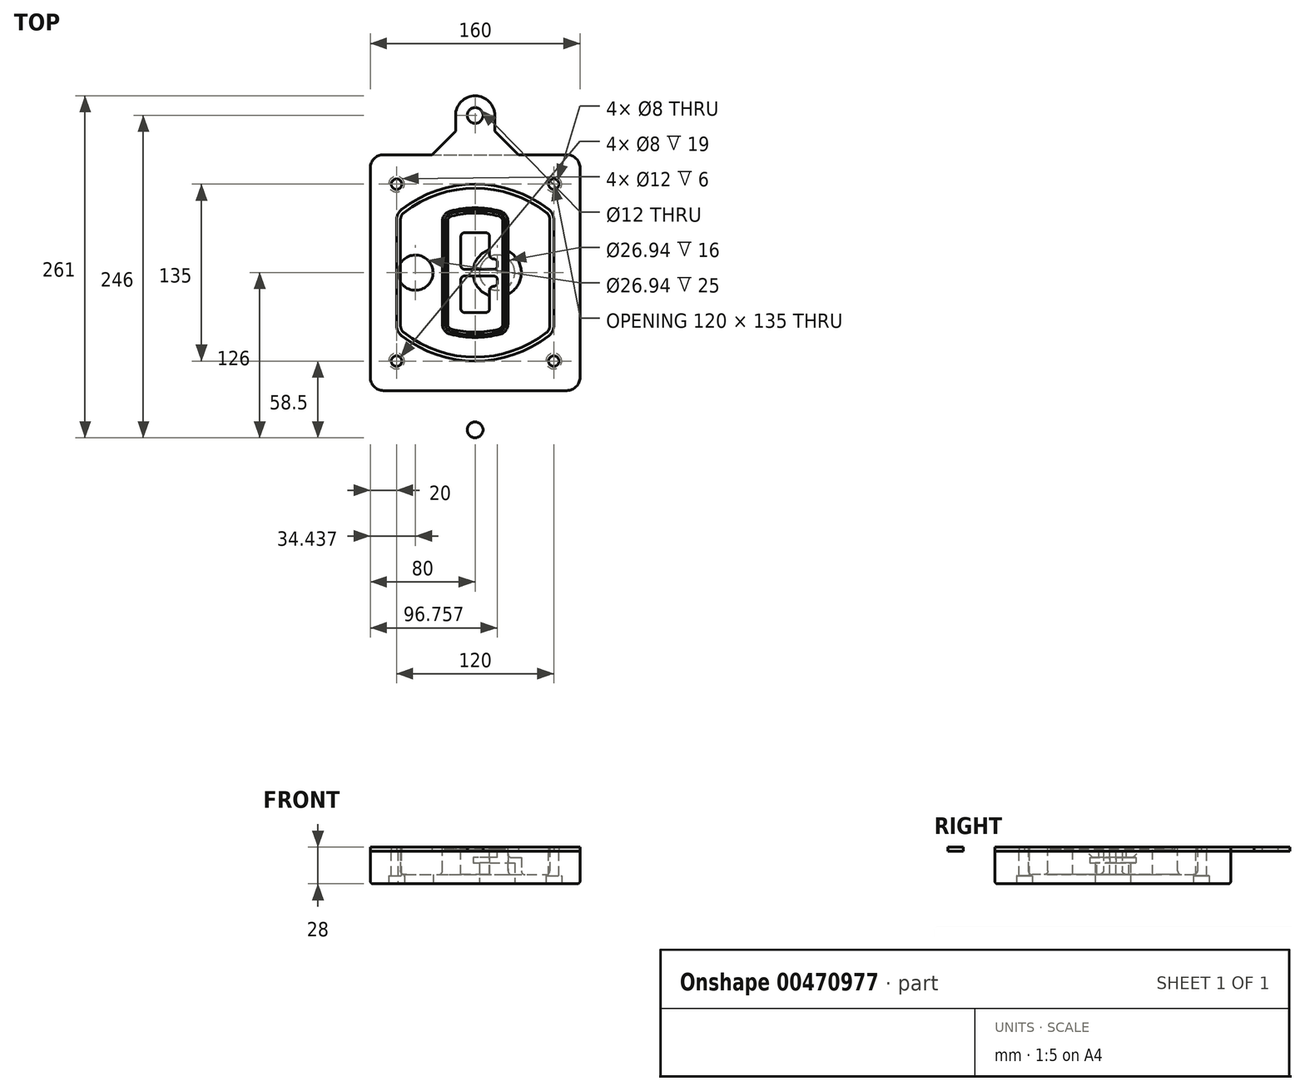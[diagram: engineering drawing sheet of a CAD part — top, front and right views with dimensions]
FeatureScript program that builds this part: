
annotation { "Feature Type Name" : "Feature", "Feature Type Description" : "" }
export const myFeature = defineFeature(function(context is Context, id is Id, definition is map)
    precondition{}
    {
        {
            var Q0;
            Q0=qCreatedBy(makeId("Top.planeOp"),FACE);
            var sketch = newSketch(context, id + "F0", { "sketchPlane" : qUnion([Q0])});
            skPoint(sketch, "E0.rect.middle", {"position": v(0, 0) * mm});
            skLineSegment(sketch, "E1.bottom", {"start": v(-70, -90) * mm, "end": v(70, -90) * mm});
            skLineSegment(sketch, "E1.top", {"start": v(-70, 90) * mm, "end": v(70, 90) * mm});
            skLineSegment(sketch, "E1.left", {"start": v(-80, -80) * mm, "end": v(-80, 80) * mm});
            skLineSegment(sketch, "E1.right", {"start": v(80, -80) * mm, "end": v(80, 80) * mm});
            skLineSegment(sketch, "E2", {"start": v(-80, 90) * mm, "end": v(80, -90) * mm, "construction": true});
            skLineSegment(sketch, "E3", {"start": v(80, 90) * mm, "end": v(-80, -90) * mm, "construction": true});
            skCircle(sketch, "E4", {"center": v(-60, 67.5) * mm, "radius": 4 * mm});
            skCircle(sketch, "E5", {"center": v(60, 67.5) * mm, "radius": 4 * mm});
            skCircle(sketch, "E6", {"center": v(60, -67.5) * mm, "radius": 4 * mm});
            skCircle(sketch, "E7", {"center": v(-60, -67.5) * mm, "radius": 4 * mm});
            skLineSegment(sketch, "E8", {"start": v(-60, 67.5) * mm, "end": v(60, 67.5) * mm, "construction": true});
            skLineSegment(sketch, "E9", {"start": v(60, 67.5) * mm, "end": v(60, -67.5) * mm, "construction": true});
            skLineSegment(sketch, "E10", {"start": v(60, -67.5) * mm, "end": v(-60, -67.5) * mm, "construction": true});
            skLineSegment(sketch, "E11", {"start": v(-60, -67.5) * mm, "end": v(-60, 67.5) * mm, "construction": true});
            skLineSegment(sketch, "E12", {"start": v(-60, 40.3) * mm, "end": v(-60, -40.3) * mm});
            skLineSegment(sketch, "E13", {"start": v(60, 40.3) * mm, "end": v(60, -40.3) * mm});
            skArc(sketch, "E14", {"start": v(56.15, 48.18) * mm, "mid": v(0, 67.5) * mm, "end": v(-56.15, 48.18) * mm});
            skArc(sketch, "E15", {"start": v(-56.15, -48.18) * mm, "mid": v(0, -67.5) * mm, "end": v(56.15, -48.18) * mm});
            skLineSegment(sketch, "E16", {"start": v(-60, 0) * mm, "end": v(60, 0) * mm, "construction": true});
            skPoint(sketch, "E17.visualSharp", {"position": v(-60, -45) * mm});
            skArc(sketch, "E17.filletArc", {"start": v(-60, -40.3) * mm, "mid": v(-58.99, -44.68) * mm, "end": v(-56.15, -48.18) * mm});
            skPoint(sketch, "E18.visualSharp", {"position": v(-60, 45) * mm});
            skArc(sketch, "E18.filletArc", {"start": v(-56.15, 48.18) * mm, "mid": v(-58.99, 44.68) * mm, "end": v(-60, 40.3) * mm});
            skPoint(sketch, "E19.visualSharp", {"position": v(60, 45) * mm});
            skArc(sketch, "E19.filletArc", {"start": v(60, 40.3) * mm, "mid": v(58.99, 44.68) * mm, "end": v(56.15, 48.18) * mm});
            skPoint(sketch, "E20.visualSharp", {"position": v(60, -45) * mm});
            skArc(sketch, "E20.filletArc", {"start": v(56.15, -48.18) * mm, "mid": v(58.99, -44.68) * mm, "end": v(60, -40.3) * mm});
            skPoint(sketch, "E21.visualSharp", {"position": v(-80, 90) * mm});
            skArc(sketch, "E21.filletArc", {"start": v(-70, 90) * mm, "mid": v(-77.07, 87.07) * mm, "end": v(-80, 80) * mm});
            skPoint(sketch, "E22.visualSharp", {"position": v(80, 90) * mm});
            skArc(sketch, "E22.filletArc", {"start": v(80, 80) * mm, "mid": v(77.07, 87.07) * mm, "end": v(70, 90) * mm});
            skPoint(sketch, "E23.visualSharp", {"position": v(80, -90) * mm});
            skArc(sketch, "E23.filletArc", {"start": v(70, -90) * mm, "mid": v(77.07, -87.07) * mm, "end": v(80, -80) * mm});
            skPoint(sketch, "E24.visualSharp", {"position": v(-80, -90) * mm});
            skArc(sketch, "E24.filletArc", {"start": v(-80, -80) * mm, "mid": v(-77.07, -87.07) * mm, "end": v(-70, -90) * mm});
            skArc(sketch, "E25.0", {"start": v(57, 40.3) * mm, "mid": v(56.3, 43.36) * mm, "end": v(54.3, 45.81) * mm});
            skLineSegment(sketch, "E25.1", {"start": v(57, 40.3) * mm, "end": v(57, -40.3) * mm});
            skArc(sketch, "E25.2", {"start": v(54.3, -45.81) * mm, "mid": v(56.3, -43.36) * mm, "end": v(57, -40.3) * mm});
            skArc(sketch, "E25.3", {"start": v(-54.3, -45.81) * mm, "mid": v(0, -64.5) * mm, "end": v(54.3, -45.81) * mm});
            skArc(sketch, "E25.4", {"start": v(-57, -40.3) * mm, "mid": v(-56.3, -43.36) * mm, "end": v(-54.3, -45.81) * mm});
            skArc(sketch, "E25.5", {"start": v(54.3, 45.81) * mm, "mid": v(0, 64.5) * mm, "end": v(-54.3, 45.81) * mm});
            skLineSegment(sketch, "E25.6", {"start": v(-57, 40.3) * mm, "end": v(-57, -40.3) * mm});
            skArc(sketch, "E25.7", {"start": v(-54.3, 45.81) * mm, "mid": v(-56.3, 43.36) * mm, "end": v(-57, 40.3) * mm});
            skArc(sketch, "E26.0", {"start": v(-58.62, 51.33) * mm, "mid": v(-62.58, 46.43) * mm, "end": v(-64, 40.3) * mm});
            skArc(sketch, "E26.1", {"start": v(58.62, 51.33) * mm, "mid": v(0, 71.5) * mm, "end": v(-58.62, 51.33) * mm});
            skArc(sketch, "E26.2", {"start": v(64, 40.3) * mm, "mid": v(62.58, 46.43) * mm, "end": v(58.62, 51.33) * mm});
            skLineSegment(sketch, "E26.3", {"start": v(64, 40.3) * mm, "end": v(64, -40.3) * mm});
            skArc(sketch, "E26.4", {"start": v(58.62, -51.33) * mm, "mid": v(62.58, -46.43) * mm, "end": v(64, -40.3) * mm});
            skLineSegment(sketch, "E26.5", {"start": v(-64, 40.3) * mm, "end": v(-64, -40.3) * mm});
            skArc(sketch, "E26.6", {"start": v(-58.62, -51.33) * mm, "mid": v(0, -71.5) * mm, "end": v(58.62, -51.33) * mm});
            skArc(sketch, "E26.7", {"start": v(-64, -40.3) * mm, "mid": v(-62.58, -46.43) * mm, "end": v(-58.62, -51.33) * mm});
            skSolve(sketch);
        }
        {
            var Q0;
            Q0=makeQuery(id+"F0.imprint","IMPRINT",FACE,{"disambiguationData":[TD([[makeQuery(id+"F0.imprint","IMPRINT",EDGE,{"derivedFrom":sQuery(id+"F0.wireOp",EDGE,"E1.bottom")}),1.0]])]});
            var Q1;
            Q1=makeQuery(id+"F0.imprint","IMPRINT",FACE,{"disambiguationData":[TD([[makeQuery(id+"F0.imprint","IMPRINT",EDGE,{"derivedFrom":sQuery(id+"F0.wireOp",EDGE,"E12")}),1.0]])]});
            var Q2;
            Q2=makeQuery(id+"F0.imprint","IMPRINT",FACE,{"disambiguationData":[TD([[makeQuery(id+"F0.imprint","IMPRINT",EDGE,{"derivedFrom":sQuery(id+"F0.wireOp",EDGE,"E25.0")}),1.0]])]});
            var Q3;
            Q3=makeQuery(id+"F0.imprint","IMPRINT",FACE,{"disambiguationData":[TD([[makeQuery(id+"F0.imprint","IMPRINT",EDGE,{"derivedFrom":sQuery(id+"F0.wireOp",EDGE,"E12")}),-1.0]])]});
            extrude(context, id + "F1", {"entities" : qUnion([Q0, Q1, Q2, Q3]), "oppositeDirection" : true, "depth" : 25 * mm});
        }
        {
            var Q0;
            Q0=makeQuery(id+"F0.imprint","IMPRINT",FACE,{"disambiguationData":[TD([[makeQuery(id+"F0.imprint","IMPRINT",EDGE,{"derivedFrom":sQuery(id+"F0.wireOp",EDGE,"E12")}),1.0]])]});
            extrude(context, id + "F2", {"entities" : qUnion([Q0]), "operationType" : NewBodyOperationType.ADD, "depth" : 3 * mm});
        }
        {
            var Q0;
            Q0=makeQuery(id+"F0.imprint","IMPRINT",FACE,{"disambiguationData":[TD([[makeQuery(id+"F0.imprint","IMPRINT",EDGE,{"derivedFrom":sQuery(id+"F0.wireOp",EDGE,"E25.0")}),1.0]])]});
            extrude(context, id + "F3", {"entities" : qUnion([Q0]), "operationType" : NewBodyOperationType.REMOVE, "oppositeDirection" : true, "depth" : 18 * mm});
        }
        {
            var Q0;
            Q0=makeQuery(id+"F2.opExtrude","CAP_FACE",FACE,{"disambiguationData":[OSD([sQuery(id+"F0.wireOp",EDGE,"E12"),sQuery(id+"F0.wireOp",EDGE,"E13"),sQuery(id+"F0.wireOp",EDGE,"E14"),sQuery(id+"F0.wireOp",EDGE,"E15"),sQuery(id+"F0.wireOp",EDGE,"E17.filletArc"),sQuery(id+"F0.wireOp",EDGE,"E18.filletArc"),sQuery(id+"F0.wireOp",EDGE,"E19.filletArc"),sQuery(id+"F0.wireOp",EDGE,"E20.filletArc"),sQuery(id+"F0.wireOp",EDGE,"E25.0"),sQuery(id+"F0.wireOp",EDGE,"E25.1"),sQuery(id+"F0.wireOp",EDGE,"E25.2"),sQuery(id+"F0.wireOp",EDGE,"E25.3"),sQuery(id+"F0.wireOp",EDGE,"E25.4"),sQuery(id+"F0.wireOp",EDGE,"E25.5"),sQuery(id+"F0.wireOp",EDGE,"E25.6"),sQuery(id+"F0.wireOp",EDGE,"E25.7")])],"isStart":false});
            var sketch = newSketch(context, id + "F4", { "sketchPlane" : qUnion([Q0])});
            skArc(sketch, "E27.0", {"start": v(-19.08, -46.97) * mm, "mid": v(0, -49.5) * mm, "end": v(19.08, -46.97) * mm});
            skArc(sketch, "E28.0", {"start": v(19.08, 46.97) * mm, "mid": v(0, 49.5) * mm, "end": v(-19.08, 46.97) * mm});
            skLineSegment(sketch, "E29", {"start": v(-25, 39.25) * mm, "end": v(-25, -39.25) * mm});
            skLineSegment(sketch, "E30", {"start": v(25, 39.25) * mm, "end": v(25, -39.25) * mm});
            skLineSegment(sketch, "E31", {"start": v(-25, 45.1) * mm, "end": v(25, 45.1) * mm, "construction": true});
            skLineSegment(sketch, "E32", {"start": v(-25, -45.1) * mm, "end": v(25, -45.1) * mm, "construction": true});
            skPoint(sketch, "E33.visualSharp", {"position": v(-25, 45.1) * mm});
            skArc(sketch, "E33.filletArc", {"start": v(-19.08, 46.97) * mm, "mid": v(-23.35, 44.11) * mm, "end": v(-25, 39.25) * mm});
            skPoint(sketch, "E34.visualSharp", {"position": v(25, 45.1) * mm});
            skArc(sketch, "E34.filletArc", {"start": v(25, 39.25) * mm, "mid": v(23.35, 44.11) * mm, "end": v(19.08, 46.97) * mm});
            skPoint(sketch, "E35.visualSharp", {"position": v(25, -45.1) * mm});
            skArc(sketch, "E35.filletArc", {"start": v(19.08, -46.97) * mm, "mid": v(23.35, -44.11) * mm, "end": v(25, -39.25) * mm});
            skPoint(sketch, "E36.visualSharp", {"position": v(-25, -45.1) * mm});
            skArc(sketch, "E36.filletArc", {"start": v(-25, -39.25) * mm, "mid": v(-23.35, -44.11) * mm, "end": v(-19.08, -46.97) * mm});
            skArc(sketch, "E37.0", {"start": v(54.3, 45.81) * mm, "mid": v(0, 64.5) * mm, "end": v(-54.3, 45.81) * mm});
            skArc(sketch, "E37.1", {"start": v(-54.3, 45.81) * mm, "mid": v(-56.3, 43.36) * mm, "end": v(-57, 40.3) * mm});
            skLineSegment(sketch, "E37.2", {"start": v(-57, 40.3) * mm, "end": v(-57, -40.3) * mm});
            skArc(sketch, "E37.3", {"start": v(-57, -40.3) * mm, "mid": v(-56.3, -43.36) * mm, "end": v(-54.3, -45.81) * mm});
            skArc(sketch, "E37.4", {"start": v(-54.3, -45.81) * mm, "mid": v(0, -64.5) * mm, "end": v(54.3, -45.81) * mm});
            skArc(sketch, "E37.5", {"start": v(54.3, -45.81) * mm, "mid": v(56.3, -43.36) * mm, "end": v(57, -40.3) * mm});
            skLineSegment(sketch, "E37.6", {"start": v(57, 40.3) * mm, "end": v(57, -40.3) * mm});
            skArc(sketch, "E37.7", {"start": v(57, 40.3) * mm, "mid": v(56.3, 43.36) * mm, "end": v(54.3, 45.81) * mm});
            skLineSegment(sketch, "E38.0", {"start": v(23, 39.25) * mm, "end": v(23, -39.25) * mm});
            skArc(sketch, "E38.1", {"start": v(18.56, -45.04) * mm, "mid": v(21.76, -42.9) * mm, "end": v(23, -39.25) * mm});
            skArc(sketch, "E38.2", {"start": v(-18.56, -45.04) * mm, "mid": v(0, -47.5) * mm, "end": v(18.56, -45.04) * mm});
            skArc(sketch, "E38.3", {"start": v(-23, -39.25) * mm, "mid": v(-21.76, -42.9) * mm, "end": v(-18.56, -45.04) * mm});
            skLineSegment(sketch, "E38.4", {"start": v(-23, 39.25) * mm, "end": v(-23, -39.25) * mm});
            skArc(sketch, "E38.5", {"start": v(23, 39.25) * mm, "mid": v(21.76, 42.9) * mm, "end": v(18.56, 45.04) * mm});
            skArc(sketch, "E38.6", {"start": v(-18.56, 45.04) * mm, "mid": v(-21.76, 42.9) * mm, "end": v(-23, 39.25) * mm});
            skArc(sketch, "E38.7", {"start": v(18.56, 45.04) * mm, "mid": v(0, 47.5) * mm, "end": v(-18.56, 45.04) * mm});
            skArc(sketch, "E39.0", {"start": v(21, 39.25) * mm, "mid": v(20.18, 41.68) * mm, "end": v(18.04, 43.1) * mm});
            skLineSegment(sketch, "E39.1", {"start": v(21, 39.25) * mm, "end": v(21, -39.25) * mm});
            skArc(sketch, "E39.2", {"start": v(18.04, -43.1) * mm, "mid": v(20.18, -41.68) * mm, "end": v(21, -39.25) * mm});
            skArc(sketch, "E39.3", {"start": v(-18.04, -43.1) * mm, "mid": v(0, -45.5) * mm, "end": v(18.04, -43.1) * mm});
            skArc(sketch, "E39.4", {"start": v(-21, -39.25) * mm, "mid": v(-20.18, -41.68) * mm, "end": v(-18.04, -43.1) * mm});
            skArc(sketch, "E39.5", {"start": v(18.04, 43.1) * mm, "mid": v(0, 45.5) * mm, "end": v(-18.04, 43.1) * mm});
            skLineSegment(sketch, "E39.6", {"start": v(-21, 39.25) * mm, "end": v(-21, -39.25) * mm});
            skArc(sketch, "E39.7", {"start": v(-18.04, 43.1) * mm, "mid": v(-20.18, 41.68) * mm, "end": v(-21, 39.25) * mm});
            skLineSegment(sketch, "E40", {"start": v(-25, 0) * mm, "end": v(25, 0) * mm, "construction": true});
            skLineSegment(sketch, "E41", {"start": v(-11, 5.5) * mm, "end": v(-11, 27.5) * mm});
            skLineSegment(sketch, "E42", {"start": v(-8, 30.5) * mm, "end": v(8, 30.5) * mm});
            skLineSegment(sketch, "E43", {"start": v(11, 27.5) * mm, "end": v(11, 13.5) * mm});
            skLineSegment(sketch, "E44", {"start": v(14, 10.5) * mm, "end": v(14, 10.5) * mm});
            skLineSegment(sketch, "E45", {"start": v(17, 7.5) * mm, "end": v(17, 5.5) * mm});
            skLineSegment(sketch, "E46", {"start": v(14, 2.5) * mm, "end": v(-8, 2.5) * mm});
            skPoint(sketch, "E47.visualSharp", {"position": v(-11, 30.5) * mm});
            skArc(sketch, "E47.filletArc", {"start": v(-8, 30.5) * mm, "mid": v(-10.12, 29.62) * mm, "end": v(-11, 27.5) * mm});
            skPoint(sketch, "E48.visualSharp", {"position": v(11, 30.5) * mm});
            skArc(sketch, "E48.filletArc", {"start": v(11, 27.5) * mm, "mid": v(10.12, 29.62) * mm, "end": v(8, 30.5) * mm});
            skPoint(sketch, "E49.visualSharp", {"position": v(11, 10.5) * mm});
            skArc(sketch, "E49.filletArc", {"start": v(11, 13.5) * mm, "mid": v(11.88, 11.38) * mm, "end": v(14, 10.5) * mm});
            skPoint(sketch, "E50.visualSharp", {"position": v(17, 10.5) * mm});
            skArc(sketch, "E50.filletArc", {"start": v(17, 7.5) * mm, "mid": v(16.12, 9.62) * mm, "end": v(14, 10.5) * mm});
            skPoint(sketch, "E51.visualSharp", {"position": v(17, 2.5) * mm});
            skArc(sketch, "E51.filletArc", {"start": v(14, 2.5) * mm, "mid": v(16.12, 3.38) * mm, "end": v(17, 5.5) * mm});
            skPoint(sketch, "E52.visualSharp", {"position": v(-11, 2.5) * mm});
            skArc(sketch, "E52.filletArc", {"start": v(-11, 5.5) * mm, "mid": v(-10.12, 3.38) * mm, "end": v(-8, 2.5) * mm});
            skLineSegment(sketch, "E53.0.MirrorCS", {"start": v(14, -2.5) * mm, "end": v(-8, -2.5) * mm});
            skArc(sketch, "E54.0.MirrorCS", {"start": v(-11, -5.5) * mm, "mid": v(-10.12, -3.38) * mm, "end": v(-8, -2.5) * mm});
            skLineSegment(sketch, "E55.0.MirrorCS", {"start": v(-11, -5.5) * mm, "end": v(-11, -27.5) * mm});
            skArc(sketch, "E56.0.MirrorCS", {"start": v(-8, -30.5) * mm, "mid": v(-10.12, -29.62) * mm, "end": v(-11, -27.5) * mm});
            skLineSegment(sketch, "E57.0.MirrorCS", {"start": v(-8, -30.5) * mm, "end": v(8, -30.5) * mm});
            skArc(sketch, "E58.0.MirrorCS", {"start": v(11, -27.5) * mm, "mid": v(10.12, -29.62) * mm, "end": v(8, -30.5) * mm});
            skLineSegment(sketch, "E59.0.MirrorCS", {"start": v(11, -27.5) * mm, "end": v(11, -13.5) * mm});
            skArc(sketch, "E60.0.MirrorCS", {"start": v(11, -13.5) * mm, "mid": v(11.88, -11.38) * mm, "end": v(14, -10.5) * mm});
            skArc(sketch, "E61.0.MirrorCS", {"start": v(17, -7.5) * mm, "mid": v(16.12, -9.62) * mm, "end": v(14, -10.5) * mm});
            skLineSegment(sketch, "E62.0.MirrorCS", {"start": v(17, -7.5) * mm, "end": v(17, -5.5) * mm});
            skArc(sketch, "E63.0.MirrorCS", {"start": v(14, -2.5) * mm, "mid": v(16.12, -3.38) * mm, "end": v(17, -5.5) * mm});
            skSolve(sketch);
        }
        {
            var Q0;
            Q0=makeQuery(id+"F4.imprint","IMPRINT",FACE,{"disambiguationData":[TD([[makeQuery(id+"F4.imprint","IMPRINT",EDGE,{"derivedFrom":sQuery(id+"F4.wireOp",EDGE,"E27.0")}),1.0]])]});
            var Q1;
            Q1=makeQuery(id+"F4.imprint","IMPRINT",FACE,{"disambiguationData":[TD([[makeQuery(id+"F4.imprint","IMPRINT",EDGE,{"derivedFrom":sQuery(id+"F4.wireOp",EDGE,"E38.0")}),-1.0]])]});
            var Q2;
            Q2=makeQuery(id+"F4.imprint","IMPRINT",FACE,{"disambiguationData":[TD([[makeQuery(id+"F4.imprint","IMPRINT",EDGE,{"derivedFrom":sQuery(id+"F4.wireOp",EDGE,"E39.0")}),1.0]])]});
            extrude(context, id + "F5", {"entities" : qUnion([Q0, Q1, Q2]), "operationType" : NewBodyOperationType.ADD, "endBound" : BoundingType.UP_TO_NEXT, "oppositeDirection" : true, "depth" : 25 * mm});
        }
        {
            var Q0;
            Q0=makeQuery(id+"F4.imprint","IMPRINT",FACE,{"disambiguationData":[TD([[makeQuery(id+"F4.imprint","IMPRINT",EDGE,{"derivedFrom":sQuery(id+"F4.wireOp",EDGE,"E38.0")}),-1.0]])]});
            extrude(context, id + "F6", {"entities" : qUnion([Q0]), "operationType" : NewBodyOperationType.REMOVE, "oppositeDirection" : true, "depth" : 2 * mm});
        }
        {
            var Q0;
            Q0=makeQuery(id+"F1.opExtrude","CAP_FACE",FACE,{"disambiguationData":[OSD([sQuery(id+"F0.wireOp",EDGE,"E1.bottom"),sQuery(id+"F0.wireOp",EDGE,"E1.top"),sQuery(id+"F0.wireOp",EDGE,"E1.left"),sQuery(id+"F0.wireOp",EDGE,"E1.right"),sQuery(id+"F0.wireOp",EDGE,"E4"),sQuery(id+"F0.wireOp",EDGE,"E5"),sQuery(id+"F0.wireOp",EDGE,"E6"),sQuery(id+"F0.wireOp",EDGE,"E7"),sQuery(id+"F0.wireOp",EDGE,"E21.filletArc"),sQuery(id+"F0.wireOp",EDGE,"E22.filletArc"),sQuery(id+"F0.wireOp",EDGE,"E23.filletArc"),sQuery(id+"F0.wireOp",EDGE,"E24.filletArc")])],"isStart":false});
            var sketch = newSketch(context, id + "F7", { "sketchPlane" : qUnion([Q0])});
            skCircle(sketch, "E64", {"center": v(16.76, 0) * mm, "radius": 13.47 * mm});
            skCircle(sketch, "E65", {"center": v(-45.56, 0) * mm, "radius": 13.47 * mm});
            skLineSegment(sketch, "E66", {"start": v(80, 0) * mm, "end": v(-80, 0) * mm});
            skCircle(sketch, "E67", {"center": v(16.76, 0) * mm, "radius": 18.47 * mm});
            skCircle(sketch, "E68", {"center": v(60, -67.5) * mm, "radius": 6 * mm});
            skCircle(sketch, "E69", {"center": v(-60, -67.5) * mm, "radius": 6 * mm});
            skCircle(sketch, "E70", {"center": v(-60, 67.5) * mm, "radius": 6 * mm});
            skCircle(sketch, "E71", {"center": v(60, 67.5) * mm, "radius": 6 * mm});
            skSolve(sketch);
        }
        {
            var Q0;
            {var subQ1=sQuery(id+"F7.wireOp",EDGE,"E66");var subQ4=sQuery(id+"F7.wireOp",EDGE,"E64");var subQ6=makeQuery(id+"F7.imprint","INTERSECT",VERTEX,{"disambiguationData":[OD(0.0)],"derivedFrom":[subQ4,subQ1]});Q0=makeQuery(id+"F7.imprint","IMPRINT",FACE,{"disambiguationData":[TD([[makeQuery(id+"F7.imprint","IMPRINT",EDGE,{"disambiguationData":[TD([[subQ6,-1.0]])],"derivedFrom":subQ4}),-1.0]])]});}
            var Q1;
            {var subQ0=sQuery(id+"F7.wireOp",EDGE,"E66");var subQ1=sQuery(id+"F7.wireOp",EDGE,"E64");var subQ3=makeQuery(id+"F7.imprint","INTERSECT",VERTEX,{"disambiguationData":[OD(0.0)],"derivedFrom":[subQ1,subQ0]});Q1=makeQuery(id+"F7.imprint","IMPRINT",FACE,{"disambiguationData":[TD([[makeQuery(id+"F7.imprint","IMPRINT",EDGE,{"disambiguationData":[TD([[subQ3,-1.0]])],"derivedFrom":subQ1}),1.0]])]});}
            var Q2;
            {var subQ0=sQuery(id+"F7.wireOp",EDGE,"E66");var subQ1=sQuery(id+"F7.wireOp",EDGE,"E64");var subQ3=makeQuery(id+"F7.imprint","INTERSECT",VERTEX,{"disambiguationData":[OD(0.0)],"derivedFrom":[subQ1,subQ0]});Q2=makeQuery(id+"F7.imprint","IMPRINT",FACE,{"disambiguationData":[TD([[makeQuery(id+"F7.imprint","IMPRINT",EDGE,{"disambiguationData":[TD([[subQ3,1.0]])],"derivedFrom":subQ1}),1.0]])]});}
            var Q3;
            {var subQ1=sQuery(id+"F7.wireOp",EDGE,"E66");var subQ4=sQuery(id+"F7.wireOp",EDGE,"E64");var subQ6=makeQuery(id+"F7.imprint","INTERSECT",VERTEX,{"disambiguationData":[OD(0.0)],"derivedFrom":[subQ4,subQ1]});Q3=makeQuery(id+"F7.imprint","IMPRINT",FACE,{"disambiguationData":[TD([[makeQuery(id+"F7.imprint","IMPRINT",EDGE,{"disambiguationData":[TD([[subQ6,1.0]])],"derivedFrom":subQ4}),-1.0]])]});}
            extrude(context, id + "F8", {"entities" : qUnion([Q0, Q1, Q2, Q3]), "operationType" : NewBodyOperationType.ADD, "oppositeDirection" : true, "depth" : 20 * mm});
        }
        {
            var Q0;
            {var subQ0=sQuery(id+"F7.wireOp",EDGE,"E66");var subQ1=sQuery(id+"F7.wireOp",EDGE,"E64");var subQ3=makeQuery(id+"F7.imprint","INTERSECT",VERTEX,{"disambiguationData":[OD(0.0)],"derivedFrom":[subQ1,subQ0]});Q0=makeQuery(id+"F7.imprint","IMPRINT",FACE,{"disambiguationData":[TD([[makeQuery(id+"F7.imprint","IMPRINT",EDGE,{"disambiguationData":[TD([[subQ3,-1.0]])],"derivedFrom":subQ1}),1.0]])]});}
            var Q1;
            {var subQ0=sQuery(id+"F7.wireOp",EDGE,"E66");var subQ1=sQuery(id+"F7.wireOp",EDGE,"E64");var subQ3=makeQuery(id+"F7.imprint","INTERSECT",VERTEX,{"disambiguationData":[OD(0.0)],"derivedFrom":[subQ1,subQ0]});Q1=makeQuery(id+"F7.imprint","IMPRINT",FACE,{"disambiguationData":[TD([[makeQuery(id+"F7.imprint","IMPRINT",EDGE,{"disambiguationData":[TD([[subQ3,1.0]])],"derivedFrom":subQ1}),1.0]])]});}
            extrude(context, id + "F9", {"entities" : qUnion([Q0, Q1]), "operationType" : NewBodyOperationType.REMOVE, "oppositeDirection" : true, "depth" : 16 * mm});
        }
        {
            var Q0;
            {var subQ0=sQuery(id+"F7.wireOp",EDGE,"E66");var subQ1=sQuery(id+"F7.wireOp",EDGE,"E65");var subQ3=makeQuery(id+"F7.imprint","INTERSECT",VERTEX,{"disambiguationData":[OD(0.0)],"derivedFrom":[subQ1,subQ0]});Q0=makeQuery(id+"F7.imprint","IMPRINT",FACE,{"disambiguationData":[TD([[makeQuery(id+"F7.imprint","IMPRINT",EDGE,{"disambiguationData":[TD([[subQ3,-1.0]])],"derivedFrom":subQ1}),1.0]])]});}
            var Q1;
            {var subQ0=sQuery(id+"F7.wireOp",EDGE,"E66");var subQ1=sQuery(id+"F7.wireOp",EDGE,"E65");var subQ3=makeQuery(id+"F7.imprint","INTERSECT",VERTEX,{"disambiguationData":[OD(0.0)],"derivedFrom":[subQ1,subQ0]});Q1=makeQuery(id+"F7.imprint","IMPRINT",FACE,{"disambiguationData":[TD([[makeQuery(id+"F7.imprint","IMPRINT",EDGE,{"disambiguationData":[TD([[subQ3,1.0]])],"derivedFrom":subQ1}),1.0]])]});}
            extrude(context, id + "F10", {"entities" : qUnion([Q0, Q1]), "operationType" : NewBodyOperationType.REMOVE, "oppositeDirection" : true, "depth" : 25 * mm});
        }
        {
            var Q0;
            Q0=makeQuery(id+"F7.imprint","IMPRINT",FACE,{"disambiguationData":[TD([[makeQuery(id+"F7.imprint","IMPRINT",EDGE,{"derivedFrom":sQuery(id+"F7.wireOp",EDGE,"E68")}),1.0]])]});
            var Q1;
            Q1=makeQuery(id+"F7.imprint","IMPRINT",FACE,{"disambiguationData":[TD([[makeQuery(id+"F7.imprint","IMPRINT",EDGE,{"derivedFrom":makeQuery(id+"F1.opExtrude","CAP_EDGE",EDGE,{"disambiguationData":[OSD([sQuery(id+"F0.wireOp",EDGE,"E5")])],"isStart":false})}),-1.0]])]});
            var Q2;
            Q2=makeQuery(id+"F7.imprint","IMPRINT",FACE,{"disambiguationData":[TD([[makeQuery(id+"F7.imprint","IMPRINT",EDGE,{"derivedFrom":sQuery(id+"F7.wireOp",EDGE,"E69")}),1.0]])]});
            var Q3;
            Q3=makeQuery(id+"F7.imprint","IMPRINT",FACE,{"disambiguationData":[TD([[makeQuery(id+"F7.imprint","IMPRINT",EDGE,{"derivedFrom":makeQuery(id+"F1.opExtrude","CAP_EDGE",EDGE,{"disambiguationData":[OSD([sQuery(id+"F0.wireOp",EDGE,"E4")])],"isStart":false})}),-1.0]])]});
            var Q4;
            Q4=makeQuery(id+"F7.imprint","IMPRINT",FACE,{"disambiguationData":[TD([[makeQuery(id+"F7.imprint","IMPRINT",EDGE,{"derivedFrom":sQuery(id+"F7.wireOp",EDGE,"E70")}),1.0]])]});
            var Q5;
            Q5=makeQuery(id+"F7.imprint","IMPRINT",FACE,{"disambiguationData":[TD([[makeQuery(id+"F7.imprint","IMPRINT",EDGE,{"derivedFrom":makeQuery(id+"F1.opExtrude","CAP_EDGE",EDGE,{"disambiguationData":[OSD([sQuery(id+"F0.wireOp",EDGE,"E7")])],"isStart":false})}),-1.0]])]});
            var Q6;
            Q6=makeQuery(id+"F7.imprint","IMPRINT",FACE,{"disambiguationData":[TD([[makeQuery(id+"F7.imprint","IMPRINT",EDGE,{"derivedFrom":sQuery(id+"F7.wireOp",EDGE,"E71")}),1.0]])]});
            var Q7;
            Q7=makeQuery(id+"F7.imprint","IMPRINT",FACE,{"disambiguationData":[TD([[makeQuery(id+"F7.imprint","IMPRINT",EDGE,{"derivedFrom":makeQuery(id+"F1.opExtrude","CAP_EDGE",EDGE,{"disambiguationData":[OSD([sQuery(id+"F0.wireOp",EDGE,"E6")])],"isStart":false})}),-1.0]])]});
            extrude(context, id + "F11", {"entities" : qUnion([Q0, Q1, Q2, Q3, Q4, Q5, Q6, Q7]), "operationType" : NewBodyOperationType.REMOVE, "oppositeDirection" : true, "depth" : 6 * mm});
        }
        {
            var Q0;
            Q0=makeQuery(id+"F9.boolean.opBoolean","COPY",FACE,{"derivedFrom":makeQuery(id+"F9.opExtrude","CAP_FACE",FACE,{"disambiguationData":[OSD([sQuery(id+"F7.wireOp",EDGE,"E64")])],"isStart":false})});
            var sketch = newSketch(context, id + "F12", { "sketchPlane" : qUnion([Q0])});
            skArc(sketch, "E72.0", {"start": v(11, 17.55) * mm, "mid": v(2.57, 11.82) * mm, "end": v(-1.54, 2.5) * mm});
            skArc(sketch, "E72.1", {"start": v(-1.54, -2.5) * mm, "mid": v(2.57, -11.82) * mm, "end": v(11, -17.55) * mm});
            skLineSegment(sketch, "E73", {"start": v(-1.54, -2.5) * mm, "end": v(14, -2.5) * mm});
            skLineSegment(sketch, "E74.0", {"start": v(14, 2.5) * mm, "end": v(-1.54, 2.5) * mm});
            skArc(sketch, "E74.1", {"start": v(14, 2.5) * mm, "mid": v(16.12, 3.38) * mm, "end": v(17, 5.5) * mm});
            skLineSegment(sketch, "E74.2", {"start": v(17, 7.5) * mm, "end": v(17, 5.5) * mm});
            skArc(sketch, "E74.3", {"start": v(17, 7.5) * mm, "mid": v(16.12, 9.62) * mm, "end": v(14, 10.5) * mm});
            skArc(sketch, "E74.4", {"start": v(11, 13.5) * mm, "mid": v(11.88, 11.38) * mm, "end": v(14, 10.5) * mm});
            skLineSegment(sketch, "E74.5", {"start": v(11, 17.55) * mm, "end": v(11, 13.5) * mm});
            skLineSegment(sketch, "E74.7", {"start": v(14, -2.5) * mm, "end": v(-1.54, -2.5) * mm});
            skArc(sketch, "E74.8", {"start": v(14, -2.5) * mm, "mid": v(16.12, -3.38) * mm, "end": v(17, -5.5) * mm});
            skLineSegment(sketch, "E74.9", {"start": v(17, -7.5) * mm, "end": v(17, -5.5) * mm});
            skArc(sketch, "E74.10", {"start": v(17, -7.5) * mm, "mid": v(16.12, -9.62) * mm, "end": v(14, -10.5) * mm});
            skArc(sketch, "E74.11", {"start": v(11, -13.5) * mm, "mid": v(11.88, -11.38) * mm, "end": v(14, -10.5) * mm});
            skLineSegment(sketch, "E74.12", {"start": v(11, -17.55) * mm, "end": v(11, -13.5) * mm});
            skPoint(sketch, "E75.orphan", {"position": v(11, -27.5) * mm});
            skPoint(sketch, "E76.orphan", {"position": v(-8, -2.5) * mm});
            skPoint(sketch, "E77.orphan", {"position": v(-8, 2.5) * mm});
            skPoint(sketch, "E78.orphan", {"position": v(11, 27.5) * mm});
            skSolve(sketch);
        }
        {
            var Q0;
            {var subQ7=sQuery(id+"F12.wireOp",EDGE,"E72.0");var subQ14=sQuery(id+"F12.wireOp",EDGE,"E72.1");var subQ16=sQuery(id+"F12.wireOp",EDGE,"E74.1");var subQ18=sQuery(id+"F12.wireOp",EDGE,"E74.8");Q0=qUnion([makeQuery(id+"F12.imprint","IMPRINT",FACE,{"disambiguationData":[TD([[makeQuery(id+"F12.imprint","IMPRINT",EDGE,{"derivedFrom":subQ7}),1.0]])]}),makeQuery(id+"F12.imprint","IMPRINT",FACE,{"disambiguationData":[TD([[makeQuery(id+"F12.imprint","IMPRINT",EDGE,{"derivedFrom":subQ14}),1.0]])]}),makeQuery(id+"F12.imprint","IMPRINT",FACE,{"disambiguationData":[TD([[makeQuery(id+"F12.imprint","IMPRINT",EDGE,{"derivedFrom":subQ16}),1.0]])]}),makeQuery(id+"F12.imprint","IMPRINT",FACE,{"disambiguationData":[TD([[makeQuery(id+"F12.imprint","IMPRINT",EDGE,{"derivedFrom":subQ18}),-1.0]])]})]);}
            var Q1;
            Q1=makeQuery(id+"F5.boolean.opBoolean","SPLIT",FACE,{"disambiguationData":[TD([makeQuery(id+"F5.opExtrude","SWEPT_FACE",FACE,{"disambiguationData":[OSD([sQuery(id+"F4.wireOp",EDGE,"E41")])]})])],"derivedFrom":makeQuery(id+"F3.boolean.opBoolean","COPY",FACE,{"derivedFrom":makeQuery(id+"F3.opExtrude","CAP_FACE",FACE,{"disambiguationData":[OSD([sQuery(id+"F0.wireOp",EDGE,"E25.0"),sQuery(id+"F0.wireOp",EDGE,"E25.1"),sQuery(id+"F0.wireOp",EDGE,"E25.2"),sQuery(id+"F0.wireOp",EDGE,"E25.3"),sQuery(id+"F0.wireOp",EDGE,"E25.4"),sQuery(id+"F0.wireOp",EDGE,"E25.5"),sQuery(id+"F0.wireOp",EDGE,"E25.6"),sQuery(id+"F0.wireOp",EDGE,"E25.7")])],"isStart":false})})});
            extrude(context, id + "F13", {"entities" : qUnion([Q0]), "operationType" : NewBodyOperationType.REMOVE, "endBound" : BoundingType.UP_TO_SURFACE, "endBoundEntityFace" : qUnion([Q1]), "depth" : 25 * mm});
        }
        {
            var Q0;
            Q0=makeQuery(id+"F3.boolean.opBoolean","COPY",EDGE,{"derivedFrom":makeQuery(id+"F3.opExtrude","CAP_EDGE",EDGE,{"disambiguationData":[OSD([sQuery(id+"F0.wireOp",EDGE,"E25.6")])],"isStart":false})});
            var Q1;
            Q1=makeQuery(id+"F8.boolean.opBoolean","INTERSECT",EDGE,{"derivedFrom":[makeQuery(id+"F5.opExtrude","SWEPT_FACE",FACE,{"disambiguationData":[OSD([sQuery(id+"F4.wireOp",EDGE,"E30")])]}),makeQuery(id+"F8.opExtrude","CAP_FACE",FACE,{"disambiguationData":[OSD([sQuery(id+"F7.wireOp",EDGE,"E67")])],"isStart":false})]});
            var Q2;
            Q2=makeQuery(id+"F8.boolean.opBoolean","INTERSECT",EDGE,{"disambiguationData":[OD(1.0)],"derivedFrom":[makeQuery(id+"F5.opExtrude","SWEPT_FACE",FACE,{"disambiguationData":[OSD([sQuery(id+"F4.wireOp",EDGE,"E30")])]}),makeQuery(id+"F8.opExtrude","SWEPT_FACE",FACE,{"disambiguationData":[OSD([sQuery(id+"F7.wireOp",EDGE,"E67")])]})]});
            var Q3;
            {var subQ0=sQuery(id+"F4.wireOp",EDGE,"E30");Q3=makeQuery(id+"F8.boolean.opBoolean","SPLIT",EDGE,{"disambiguationData":[TD([makeQuery(id+"F5.opExtrude","SWEPT_FACE",FACE,{"disambiguationData":[OSD([sQuery(id+"F4.wireOp",EDGE,"E35.filletArc")])]})])],"derivedFrom":makeQuery(id+"F5.opExtrude","CAP_EDGE",EDGE,{"disambiguationData":[OSD([subQ0])],"isStart":false})});}
            var Q4;
            {var subQ0=sQuery(id+"F0.wireOp",EDGE,"E25.7");var subQ1=sQuery(id+"F0.wireOp",EDGE,"E25.1");var subQ2=sQuery(id+"F0.wireOp",EDGE,"E25.6");var subQ3=sQuery(id+"F0.wireOp",EDGE,"E25.5");var subQ4=sQuery(id+"F0.wireOp",EDGE,"E25.4");var subQ5=sQuery(id+"F0.wireOp",EDGE,"E25.0");var subQ6=sQuery(id+"F0.wireOp",EDGE,"E25.2");var subQ7=sQuery(id+"F0.wireOp",EDGE,"E25.3");Q4=makeQuery(id+"F8.boolean.opBoolean","INTERSECT",EDGE,{"derivedFrom":[makeQuery(id+"F5.boolean.opBoolean","SPLIT",FACE,{"disambiguationData":[TD([makeQuery(id+"F2.opExtrude","SWEPT_FACE",FACE,{"disambiguationData":[OSD([subQ5])]})])],"derivedFrom":makeQuery(id+"F3.boolean.opBoolean","COPY",FACE,{"derivedFrom":makeQuery(id+"F3.opExtrude","CAP_FACE",FACE,{"disambiguationData":[OSD([subQ5,subQ1,subQ6,subQ7,subQ4,subQ3,subQ2,subQ0])],"isStart":false})})}),makeQuery(id+"F8.opExtrude","SWEPT_FACE",FACE,{"disambiguationData":[OSD([sQuery(id+"F7.wireOp",EDGE,"E67")])]})]});}
            var Q5;
            Q5=makeQuery(id+"F8.boolean.opBoolean","INTERSECT",EDGE,{"disambiguationData":[OD(0.0)],"derivedFrom":[makeQuery(id+"F5.opExtrude","SWEPT_FACE",FACE,{"disambiguationData":[OSD([sQuery(id+"F4.wireOp",EDGE,"E30")])]}),makeQuery(id+"F8.opExtrude","SWEPT_FACE",FACE,{"disambiguationData":[OSD([sQuery(id+"F7.wireOp",EDGE,"E67")])]})]});
            fillet(context, id + "F14", {"entities" : qUnion([Q0, Q1, Q2, Q3, Q4, Q5]), "radius" : 3 * mm, "tangentPropagation" : true, "allowEdgeOverflow" : false});
        }
        {
            var Q0;
            Q0=makeQuery(id+"F1.opExtrude","CAP_EDGE",EDGE,{"disambiguationData":[OSD([sQuery(id+"F0.wireOp",EDGE,"E1.bottom")])],"isStart":false});
            fillet(context, id + "F15", {"entities" : qUnion([Q0]), "radius" : 2 * mm, "tangentPropagation" : true, "allowEdgeOverflow" : false});
        }
        {
            var Q0;
            {var subQ0=sQuery(id+"F0.wireOp",EDGE,"E21.filletArc");var subQ1=sQuery(id+"F0.wireOp",EDGE,"E7");var subQ2=sQuery(id+"F0.wireOp",EDGE,"E6");var subQ3=sQuery(id+"F0.wireOp",EDGE,"E5");var subQ4=sQuery(id+"F0.wireOp",EDGE,"E4");var subQ5=sQuery(id+"F0.wireOp",EDGE,"E22.filletArc");var subQ6=sQuery(id+"F0.wireOp",EDGE,"E1.bottom");var subQ7=sQuery(id+"F0.wireOp",EDGE,"E1.right");var subQ8=sQuery(id+"F0.wireOp",EDGE,"E1.top");var subQ9=sQuery(id+"F0.wireOp",EDGE,"E1.left");var subQ10=sQuery(id+"F0.wireOp",EDGE,"E23.filletArc");var subQ11=sQuery(id+"F0.wireOp",EDGE,"E24.filletArc");Q0=makeQuery(id+"F2.boolean.opBoolean","SPLIT",FACE,{"disambiguationData":[TD([makeQuery(id+"F1.opExtrude","SWEPT_FACE",FACE,{"disambiguationData":[OSD([subQ6])]})])],"derivedFrom":makeQuery(id+"F1.opExtrude","CAP_FACE",FACE,{"disambiguationData":[OSD([subQ6,subQ8,subQ9,subQ7,subQ4,subQ3,subQ2,subQ1,subQ0,subQ5,subQ10,subQ11])],"isStart":true})});}
            var sketch = newSketch(context, id + "F16", { "sketchPlane" : qUnion([Q0])});
            skCircle(sketch, "E79", {"center": v(0, 120) * mm, "radius": 6 * mm});
            skPoint(sketch, "E79.centerSnap0", {"position": v(0, 90) * mm});
            skLineSegment(sketch, "E80", {"start": v(-15, 120) * mm, "end": v(-15, 108) * mm});
            skLineSegment(sketch, "E81", {"start": v(-15, 108) * mm, "end": v(-33, 90) * mm});
            skLineSegment(sketch, "E82", {"start": v(0, 120) * mm, "end": v(0, 47.9) * mm, "construction": true});
            skPoint(sketch, "E82.endSnap0", {"position": v(0, 67.5) * mm});
            skLineSegment(sketch, "E83.MirrorCS", {"start": v(15, 108) * mm, "end": v(33, 90) * mm});
            skLineSegment(sketch, "E84.MirrorCS", {"start": v(15, 120) * mm, "end": v(15, 108) * mm});
            skArc(sketch, "E85", {"start": v(15, 120) * mm, "mid": v(0, 135) * mm, "end": v(-15, 120) * mm});
            skLineSegment(sketch, "E86", {"start": v(-80, 0) * mm, "end": v(80, 0) * mm, "construction": true});
            skPoint(sketch, "E87.MirrorP", {"position": v(0, -90) * mm});
            skCircle(sketch, "E88.MirrorC", {"center": v(0, -120) * mm, "radius": 6 * mm});
            skArc(sketch, "E89.MirrorCS", {"start": v(15, -120) * mm, "mid": v(0, -135) * mm, "end": v(-15, -120) * mm});
            skLineSegment(sketch, "E90.MirrorCS", {"start": v(-15, -120) * mm, "end": v(-15, -108) * mm});
            skLineSegment(sketch, "E91.MirrorCS", {"start": v(-15, -108) * mm, "end": v(-33, -90) * mm});
            skLineSegment(sketch, "E92.MirrorCS", {"start": v(15, -120) * mm, "end": v(15, -108) * mm});
            skLineSegment(sketch, "E93.MirrorCS", {"start": v(15, -108) * mm, "end": v(33, -90) * mm});
            skSolve(sketch);
        }
        {
            var Q0;
            Q0=makeQuery(id+"F16.imprint","IMPRINT",FACE,{"disambiguationData":[TD([[makeQuery(id+"F16.imprint","IMPRINT",EDGE,{"derivedFrom":sQuery(id+"F16.wireOp",EDGE,"E79")}),-1.0]])]});
            var Q1;
            Q1=makeQuery(id+"F16.imprint","IMPRINT",FACE,{"disambiguationData":[TD([[makeQuery(id+"F16.imprint","IMPRINT",EDGE,{"derivedFrom":makeQuery(id+"F1.opExtrude","CAP_EDGE",EDGE,{"disambiguationData":[OSD([sQuery(id+"F0.wireOp",EDGE,"E1.left")])],"isStart":true})}),-1.0]])]});
            var Q2;
            Q2=makeQuery(id+"F16.imprint","IMPRINT",FACE,{"disambiguationData":[TD([[makeQuery(id+"F16.imprint","IMPRINT",EDGE,{"derivedFrom":sQuery(id+"F16.wireOp",EDGE,"E88.MirrorC")}),1.0]])]});
            var Q3;
            Q3=makeQuery(id+"F2.opExtrude","CAP_FACE",FACE,{"disambiguationData":[OSD([sQuery(id+"F0.wireOp",EDGE,"E12"),sQuery(id+"F0.wireOp",EDGE,"E13"),sQuery(id+"F0.wireOp",EDGE,"E14"),sQuery(id+"F0.wireOp",EDGE,"E15"),sQuery(id+"F0.wireOp",EDGE,"E17.filletArc"),sQuery(id+"F0.wireOp",EDGE,"E18.filletArc"),sQuery(id+"F0.wireOp",EDGE,"E19.filletArc"),sQuery(id+"F0.wireOp",EDGE,"E20.filletArc"),sQuery(id+"F0.wireOp",EDGE,"E25.0"),sQuery(id+"F0.wireOp",EDGE,"E25.1"),sQuery(id+"F0.wireOp",EDGE,"E25.2"),sQuery(id+"F0.wireOp",EDGE,"E25.3"),sQuery(id+"F0.wireOp",EDGE,"E25.4"),sQuery(id+"F0.wireOp",EDGE,"E25.5"),sQuery(id+"F0.wireOp",EDGE,"E25.6"),sQuery(id+"F0.wireOp",EDGE,"E25.7")])],"isStart":false});
            extrude(context, id + "F17", {"entities" : qUnion([Q0, Q1, Q2]), "endBound" : BoundingType.UP_TO_SURFACE, "endBoundEntityFace" : qUnion([Q3]), "depth" : 25 * mm});
        }
    });
